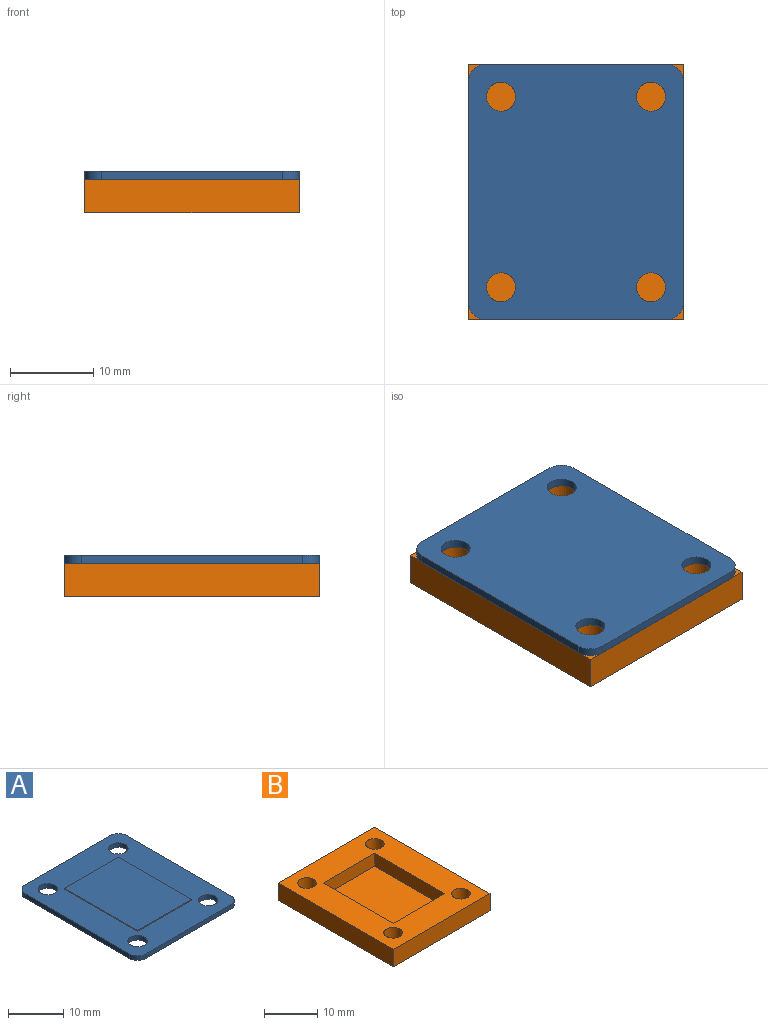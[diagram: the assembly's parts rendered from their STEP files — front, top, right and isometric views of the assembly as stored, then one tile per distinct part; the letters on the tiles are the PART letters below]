
ASSEMBLY  parts=2 mates=1
PART A: 19 faces, bbox 25.8x30.7x1.2 mm
  f0: plane 21.8x1mm, normal (0,-1,0), area 21.8mm2, adj f8,f9,f15,f18
  f1: plane 26.7x1mm, normal (1,0,0), area 26.7mm2, adj f8,f9,f15,f16
  f2: plane 21.8x1mm, normal (0,1,0), area 21.8mm2, adj f8,f9,f16,f17
  f3: cylinder r=1.75mm len=3.5mm, axis (0,0,-1), area 11mm2, adj f8,f9
  f4: cylinder r=1.75mm len=3.5mm, axis (0,0,-1), area 11mm2, adj f8,f9
  f5: cylinder r=1.75mm len=3.5mm, axis (0,0,-1), area 11mm2, adj f8,f9
  f6: cylinder r=1.75mm len=3.5mm, axis (0,0,-1), area 11mm2, adj f8,f9
  f7: plane 26.7x1mm, normal (-1,0,0), area 26.7mm2, adj f8,f9,f17,f18
  f8: plane 30.7x25.8mm, normal (0,0,1), area 492.1mm2, adj f0,f1,f2,f3,f4,f5,f6,f7
  f9: plane 30.7x25.8mm, normal (0,0,-1), area 750.1mm2, adj f0,f1,f2,f3,f4,f5,f6,f7
  f10: plane 13.8x0.2mm, normal (0,-1,0), area 2.8mm2, adj f8,f11,f13,f14
  f11: plane 18.7x0.2mm, normal (1,0,0), area 3.7mm2, adj f8,f10,f12,f14
  f12: plane 13.8x0.2mm, normal (0,1,0), area 2.8mm2, adj f8,f11,f13,f14
  f13: plane 18.7x0.2mm, normal (-1,0,0), area 3.7mm2, adj f8,f10,f12,f14
  f14: plane 18.7x13.8mm, normal (0,0,1), area 258.1mm2, adj f10,f11,f12,f13
  f15: cylinder r=2mm len=2mm, axis (0,0,1), area 3.1mm2, adj f0,f1,f8,f9
  f16: cylinder r=2mm len=2mm, axis (0,0,-1), area 3.1mm2, adj f1,f2,f8,f9
  f17: cylinder r=2mm len=2mm, axis (0,0,1), area 3.1mm2, adj f2,f7,f8,f9
  f18: cylinder r=2mm len=2mm, axis (0,0,-1), area 3.1mm2, adj f0,f7,f8,f9
PART B: 19 faces, bbox 25.8x30.7x4 mm
  f0: plane 25.8x4mm, normal (0,-1,0), area 103.2mm2, adj f1,f3,f4,f13
  f1: plane 30.7x4mm, normal (1,0,0), area 122.8mm2, adj f0,f2,f4,f13
  f2: plane 25.8x4mm, normal (0,1,0), area 103.2mm2, adj f1,f3,f4,f13
  f3: plane 30.7x4mm, normal (-1,0,0), area 122.8mm2, adj f0,f2,f4,f13
  f4: plane 30.7x25.8mm, normal (0,0,-1), area 792.1mm2, adj f0,f1,f2,f3
  f5: plane 18.7x3mm, normal (-1,0,0), area 56.1mm2, adj f6,f12,f13,f14
  f6: plane 13.8x3mm, normal (0,1,0), area 41.4mm2, adj f5,f7,f13,f14
  f7: plane 18.7x3mm, normal (1,0,0), area 56.1mm2, adj f6,f12,f13,f14
  f8: cylinder r=1.75mm len=3.5mm, axis (0,0,-1), area 33mm2, adj f13,f18
  f9: cylinder r=1.75mm len=3.5mm, axis (0,0,-1), area 33mm2, adj f13,f17
  f10: cylinder r=1.75mm len=3.5mm, axis (0,0,-1), area 33mm2, adj f13,f16
  f11: cylinder r=1.75mm len=3.5mm, axis (0,0,-1), area 33mm2, adj f13,f15
  f12: plane 13.8x3mm, normal (0,-1,0), area 41.4mm2, adj f5,f7,f13,f14
  f13: plane 30.7x25.8mm, normal (0,0,1), area 495.5mm2, adj f0,f1,f2,f3,f5,f6,f7,f8
  f14: plane 18.7x13.8mm, normal (0,0,1), area 258.1mm2, adj f5,f6,f7,f12
  f15: plane 3.5x3.5mm, normal (0,0,1), area 9.6mm2, adj f11
  f16: plane 3.5x3.5mm, normal (0,0,1), area 9.6mm2, adj f10
  f17: plane 3.5x3.5mm, normal (0,0,1), area 9.6mm2, adj f9
  f18: plane 3.5x3.5mm, normal (0,0,1), area 9.6mm2, adj f8
PLACE A rot(axis=(0,1,0),180deg) t=(-9.62,-2.9,9.72)mm
PLACE B t=(-9.65,-3.09,4.72)mm
MATE fastened A.f5 <-> B.f11  axis (0,0,1) through (-18.67,-14.56,8.72)mm
